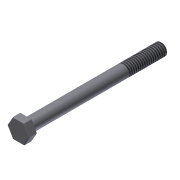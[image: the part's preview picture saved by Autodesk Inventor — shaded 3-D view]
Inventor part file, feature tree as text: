
AUTODESK INVENTOR PART (.ipt)
format: ipt  version: 2011 (Build 150239000, 239)  size: 114,688 bytes
history: native  units: in
note: dims shown in document units (in); Inventor stores cm internally (conversion verified against a paired STEP export)
features: extrude x2, sketch x2, thread x1, chamfer x1, fillet x1
ambient origin geometry x8: Origin, YZ Plane, XZ Plane, XY Plane, X Axis, Y Axis, Z Axis, Center Point
bodies: Solid1 (feature_tree)
feature tree (7):
  extrude  "Extrusion1"  Depth=3.5in TaperAngle=0.0deg
  extrude  "Extrusion2"  Depth=0.2031in TaperAngle=0.0deg
  thread  "Thread1"  [1 undecoded]
  chamfer  "Chamfer1"  Distance=0.02in Angle=45.0deg
  fillet  "Fillet1"  Radius=0.02in
  sketch  "Sketch1"  dims[d0=0.3125in d1=3.5in d2=0.0in]
  sketch  "Sketch2"  dims[d3=0.5in d4=0.2031in d5=0.0in d6=1.0in d7=0.0in d8=0.02in d9=0.125in d10=45.0deg d11=0.02in]
note: 1 required parameter value undecoded (feature->parameter linkage not recoverable at this tier; creation-order binding heuristic only, values carry confidence <= 0.55)
